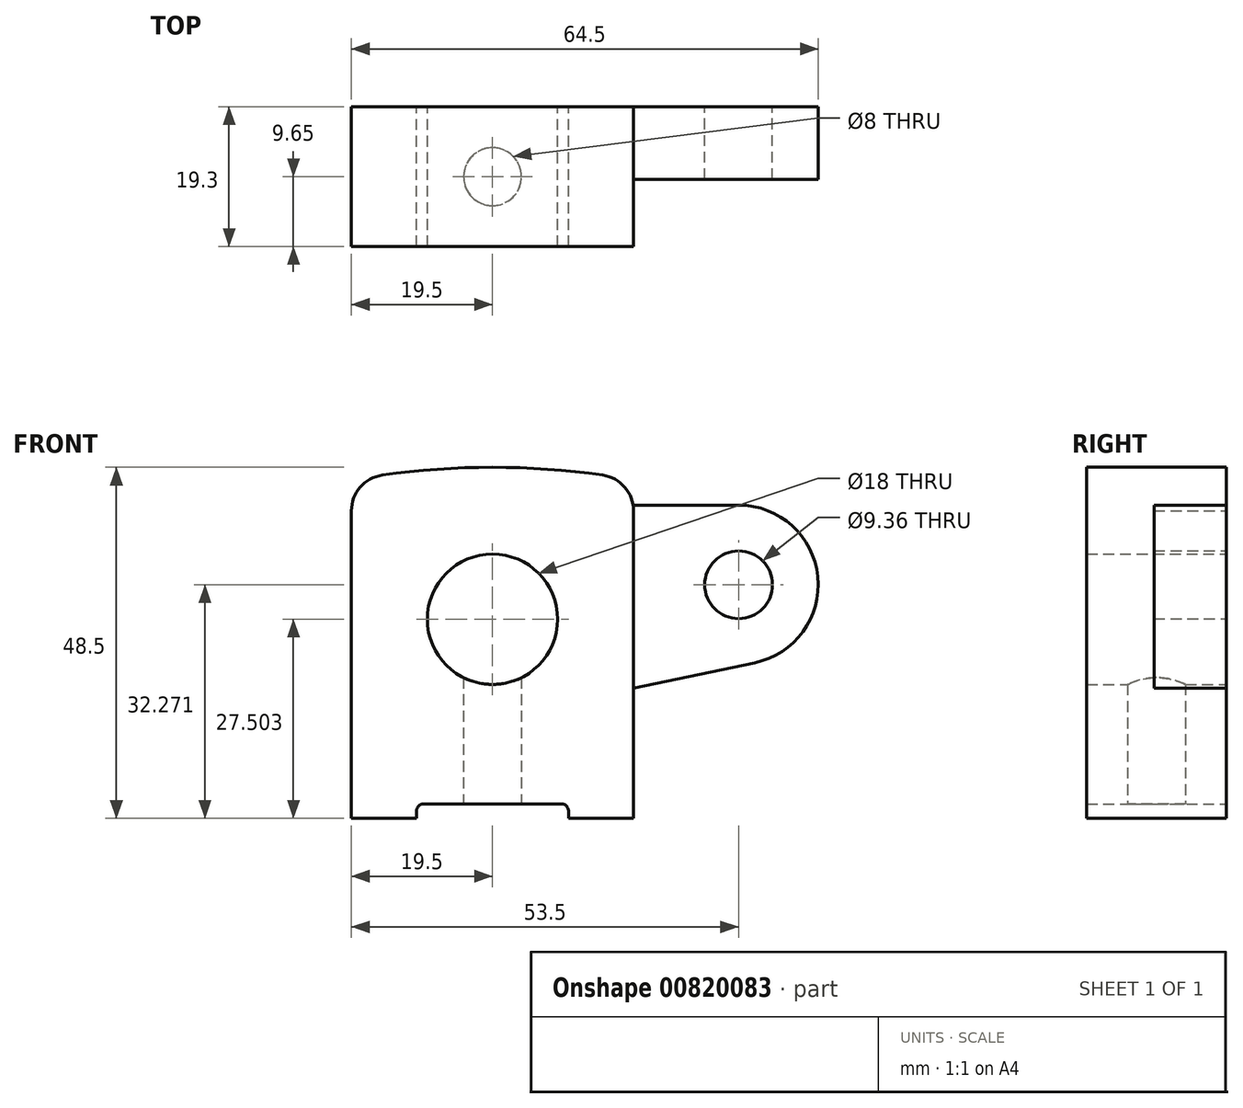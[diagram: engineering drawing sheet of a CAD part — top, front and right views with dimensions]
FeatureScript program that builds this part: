
annotation { "Feature Type Name" : "Feature", "Feature Type Description" : "" }
export const myFeature = defineFeature(function(context is Context, id is Id, definition is map)
    precondition{}
    {
        {
            var Q0;
            Q0=qCreatedBy(makeId("Front.planeOp"),FACE);
            var sketch = newSketch(context, id + "F0", { "sketchPlane" : qUnion([Q0])});
            skLineSegment(sketch, "E0.bottom", {"start": v(-19.5, 24.5) * mm, "end": v(19.5, 24.5) * mm, "construction": true});
            skLineSegment(sketch, "E0.left", {"start": v(-19.5, 20.26) * mm, "end": v(-19.5, -22.2) * mm});
            skLineSegment(sketch, "E0.right", {"start": v(19.5, 20.26) * mm, "end": v(19.5, -22.2) * mm});
            skCircle(sketch, "E1", {"center": v(0, 10.3) * mm, "radius": 9 * mm, "construction": true});
            skPoint(sketch, "E1.centerSnap0", {"position": v(0, 24.5) * mm});
            skArc(sketch, "E2", {"start": v(15.21, 25.2) * mm, "mid": v(0, 26.3) * mm, "end": v(-15.21, 25.2) * mm});
            skLineSegment(sketch, "E3", {"start": v(19.5, -22.2) * mm, "end": v(10.5, -22.2) * mm});
            skLineSegment(sketch, "E4", {"start": v(10.5, -22.2) * mm, "end": v(10.5, -20.2) * mm});
            skLineSegment(sketch, "E5", {"start": v(10.5, -20.2) * mm, "end": v(-10.5, -20.2) * mm});
            skLineSegment(sketch, "E6", {"start": v(-10.5, -20.2) * mm, "end": v(-10.5, -22.2) * mm});
            skLineSegment(sketch, "E7", {"start": v(-10.5, -22.2) * mm, "end": v(-19.5, -22.2) * mm});
            skPoint(sketch, "E8.visualSharp", {"position": v(-19.5, 24.5) * mm});
            skArc(sketch, "E8.filletArc", {"start": v(-15.21, 25.2) * mm, "mid": v(-18.28, 23.53) * mm, "end": v(-19.5, 20.26) * mm});
            skPoint(sketch, "E9.visualSharp", {"position": v(19.5, 24.5) * mm});
            skArc(sketch, "E9.filletArc", {"start": v(19.5, 20.26) * mm, "mid": v(18.28, 23.53) * mm, "end": v(15.21, 25.2) * mm});
            skCircle(sketch, "E10", {"center": v(0, 5.3) * mm, "radius": 9 * mm});
            skSolve(sketch);
        }
        {
            var Q0;
            Q0=makeQuery(id+"F0.imprint","IMPRINT",FACE,{"disambiguationData":[TD([[makeQuery(id+"F0.imprint","IMPRINT",EDGE,{"derivedFrom":sQuery(id+"F0.wireOp",EDGE,"E0.left")}),1.0]])]});
            extrude(context, id + "F1", {"entities" : qUnion([Q0]), "depth" : 19.3 * mm, "offsetDistance" : 25 * mm});
        }
        {
            var Q0;
            Q0=makeQuery(id+"F1.opExtrude","SWEPT_EDGE",EDGE,{"disambiguationData":[OSD([sQuery(id+"F0.wireOp",EDGE,"E5"),sQuery(id+"F0.wireOp",EDGE,"E6")])]});
            var Q1;
            Q1=makeQuery(id+"F1.opExtrude","SWEPT_EDGE",EDGE,{"disambiguationData":[OSD([sQuery(id+"F0.wireOp",EDGE,"E4"),sQuery(id+"F0.wireOp",EDGE,"E5")])]});
            fillet(context, id + "F2", {"entities" : qUnion([Q0, Q1]), "radius" : 1 * mm, "tangentPropagation" : true, "allowEdgeOverflow" : false});
        }
        {
            var Q0;
            Q0=qCreatedBy(makeId("Front.planeOp"),FACE);
            var sketch = newSketch(context, id + "F3", { "sketchPlane" : qUnion([Q0])});
            skCircle(sketch, "E11", {"center": v(34, 10.06) * mm, "radius": 4.68 * mm});
            skLineSegment(sketch, "E12", {"start": v(19.5, 21.06) * mm, "end": v(34, 21.06) * mm});
            skArc(sketch, "E13", {"start": v(36.25, -0.7) * mm, "mid": v(44.94, 11.2) * mm, "end": v(34, 21.06) * mm});
            skLineSegment(sketch, "E14", {"start": v(19.5, -4.2) * mm, "end": v(36.25, -0.7) * mm});
            skLineSegment(sketch, "E15", {"start": v(19.5, 21.06) * mm, "end": v(19.5, -4.2) * mm});
            skSolve(sketch);
        }
        {
            var Q0;
            Q0=qSketchRegion(id+"F3",true);
            extrude(context, id + "F4", {"entities" : qUnion([Q0]), "operationType" : NewBodyOperationType.ADD, "depth" : 10 * mm, "offsetDistance" : 25 * mm});
        }
        {
            var Q0;
            Q0=makeQuery(id+"F1.opExtrude","SWEPT_FACE",FACE,{"disambiguationData":[OSD([sQuery(id+"F0.wireOp",EDGE,"E5")])]});
            var sketch = newSketch(context, id + "F5", { "sketchPlane" : qUnion([Q0])});
            skCircle(sketch, "E16", {"center": v(0, 9.65) * mm, "radius": 4 * mm});
            skPoint(sketch, "E16.centerSnap0", {"position": v(-9.5, 9.65) * mm});
            skPoint(sketch, "E16.centerSnap1", {"position": v(0, 19.3) * mm});
            skSolve(sketch);
        }
        {
            var Q0;
            Q0=qSketchRegion(id+"F5",true);
            extrude(context, id + "F6", {"entities" : qUnion([Q0]), "operationType" : NewBodyOperationType.REMOVE, "oppositeDirection" : true, "depth" : 25 * mm, "offsetDistance" : 25 * mm});
        }
    });
